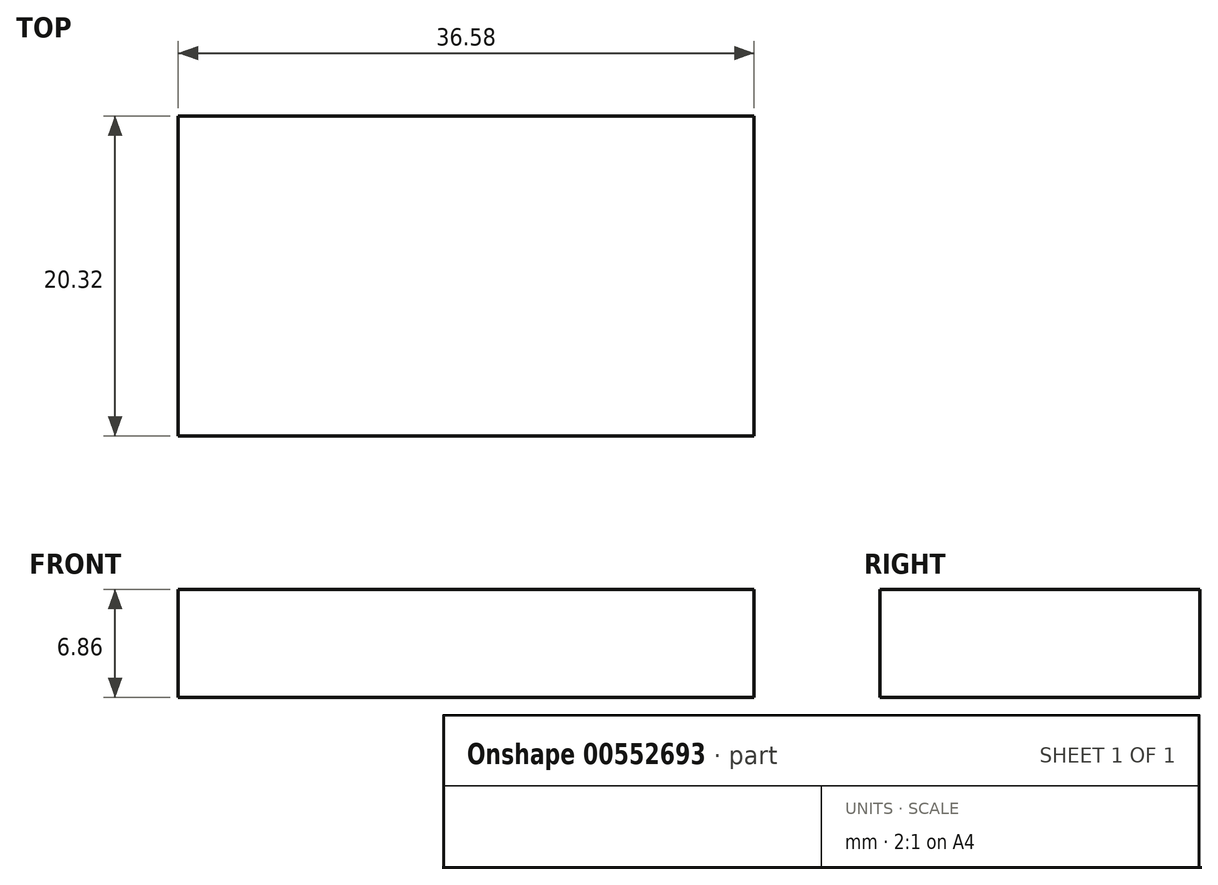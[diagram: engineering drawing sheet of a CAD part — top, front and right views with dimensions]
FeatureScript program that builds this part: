
annotation { "Feature Type Name" : "Feature", "Feature Type Description" : "" }
export const myFeature = defineFeature(function(context is Context, id is Id, definition is map)
    precondition{}
    {
        {
            var Q0;
            Q0=qCreatedBy(makeId("Top.planeOp"),FACE);
            var sketch = newSketch(context, id + "F0", { "sketchPlane" : qUnion([Q0])});
            skLineSegment(sketch, "E0.bottom", {"start": v(18.29, 10.16) * mm, "end": v(-18.29, 10.16) * mm});
            skLineSegment(sketch, "E0.top", {"start": v(18.29, -10.16) * mm, "end": v(-18.29, -10.16) * mm});
            skLineSegment(sketch, "E0.left", {"start": v(18.29, 10.16) * mm, "end": v(18.29, -10.16) * mm});
            skLineSegment(sketch, "E0.right", {"start": v(-18.29, 10.16) * mm, "end": v(-18.29, -10.16) * mm});
            skPoint(sketch, "E0.middle", {"position": v(0, 0) * mm});
            skSolve(sketch);
        }
        {
            var Q0;
            Q0=makeQuery(id+"F0.imprint","IMPRINT",FACE,{"disambiguationData":[TD([[makeQuery(id+"F0.imprint","IMPRINT",EDGE,{"derivedFrom":sQuery(id+"F0.wireOp",EDGE,"E0.bottom")}),1.0]])]});
            extrude(context, id + "F1", {"entities" : qUnion([Q0]), "depth" : 6.86 * mm, "offsetDistance" : 25.4 * mm});
        }
    });
